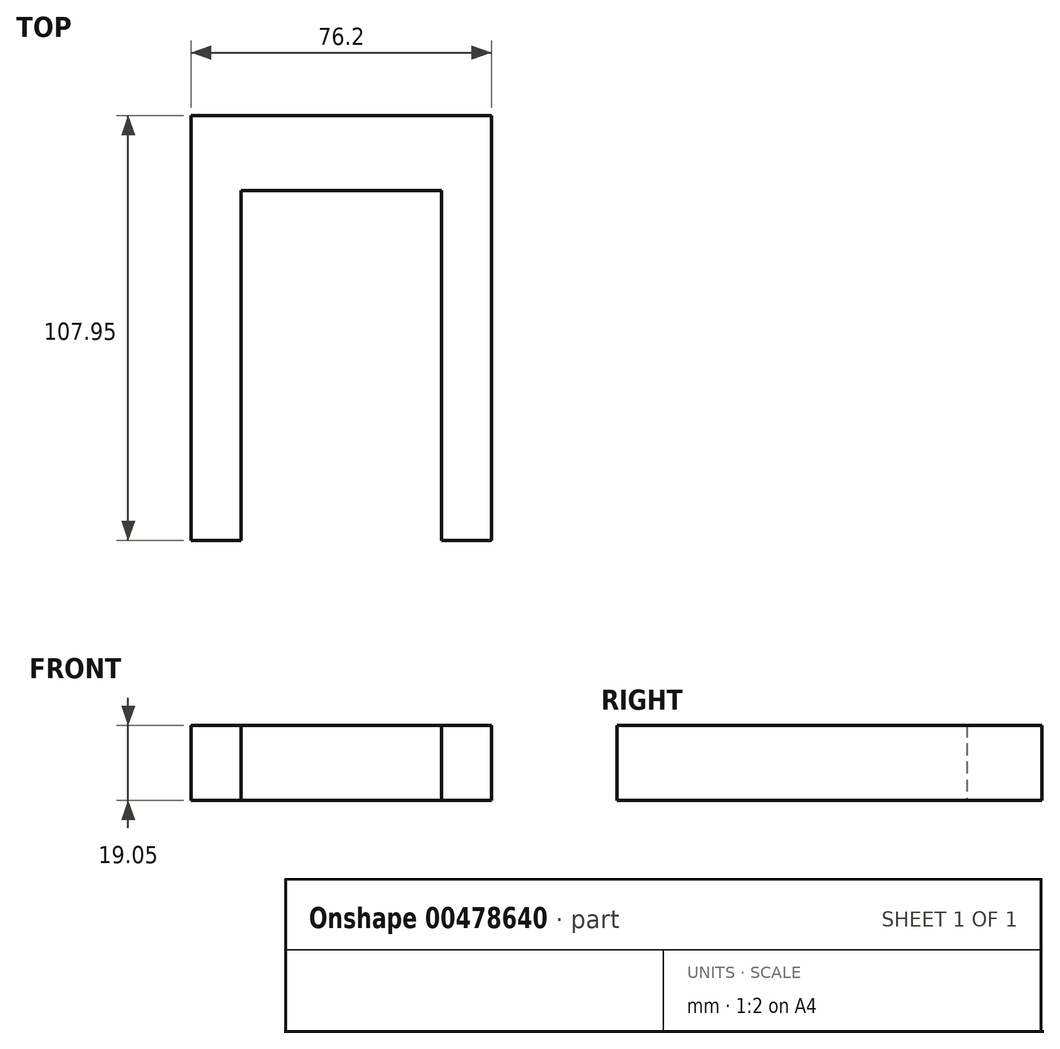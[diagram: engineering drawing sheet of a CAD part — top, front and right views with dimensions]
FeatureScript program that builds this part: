
annotation { "Feature Type Name" : "Feature", "Feature Type Description" : "" }
export const myFeature = defineFeature(function(context is Context, id is Id, definition is map)
    precondition{}
    {
        {
            var Q0;
            Q0=qCreatedBy(makeId("Top.planeOp"),FACE);
            var sketch = newSketch(context, id + "F0", { "sketchPlane" : qUnion([Q0])});
            skLineSegment(sketch, "E0", {"start": v(-92.65, 107.95) * mm, "end": v(-16.45, 107.95) * mm});
            skLineSegment(sketch, "E1", {"start": v(-92.65, 107.95) * mm, "end": v(-92.65, 0) * mm});
            skLineSegment(sketch, "E2", {"start": v(-92.65, 0) * mm, "end": v(-79.95, 0) * mm});
            skLineSegment(sketch, "E3", {"start": v(-29.15, 0) * mm, "end": v(-16.45, 0) * mm});
            skLineSegment(sketch, "E4", {"start": v(-16.45, 0) * mm, "end": v(-16.45, 107.95) * mm});
            skLineSegment(sketch, "E5", {"start": v(-79.95, 0) * mm, "end": v(-79.95, 88.9) * mm});
            skLineSegment(sketch, "E6", {"start": v(-29.15, 0) * mm, "end": v(-29.15, 88.9) * mm});
            skLineSegment(sketch, "E7", {"start": v(-29.15, 88.9) * mm, "end": v(-79.95, 88.9) * mm});
            skSolve(sketch);
        }
        {
            var Q0;
            Q0=makeQuery(id+"F0.imprint","IMPRINT",FACE,{"disambiguationData":[TD([[makeQuery(id+"F0.imprint","IMPRINT",EDGE,{"derivedFrom":sQuery(id+"F0.wireOp",EDGE,"E0")}),-1.0]])]});
            extrude(context, id + "F1", {"entities" : qUnion([Q0]), "depth" : 19.05 * mm, "offsetDistance" : 25.4 * mm});
        }
    });
